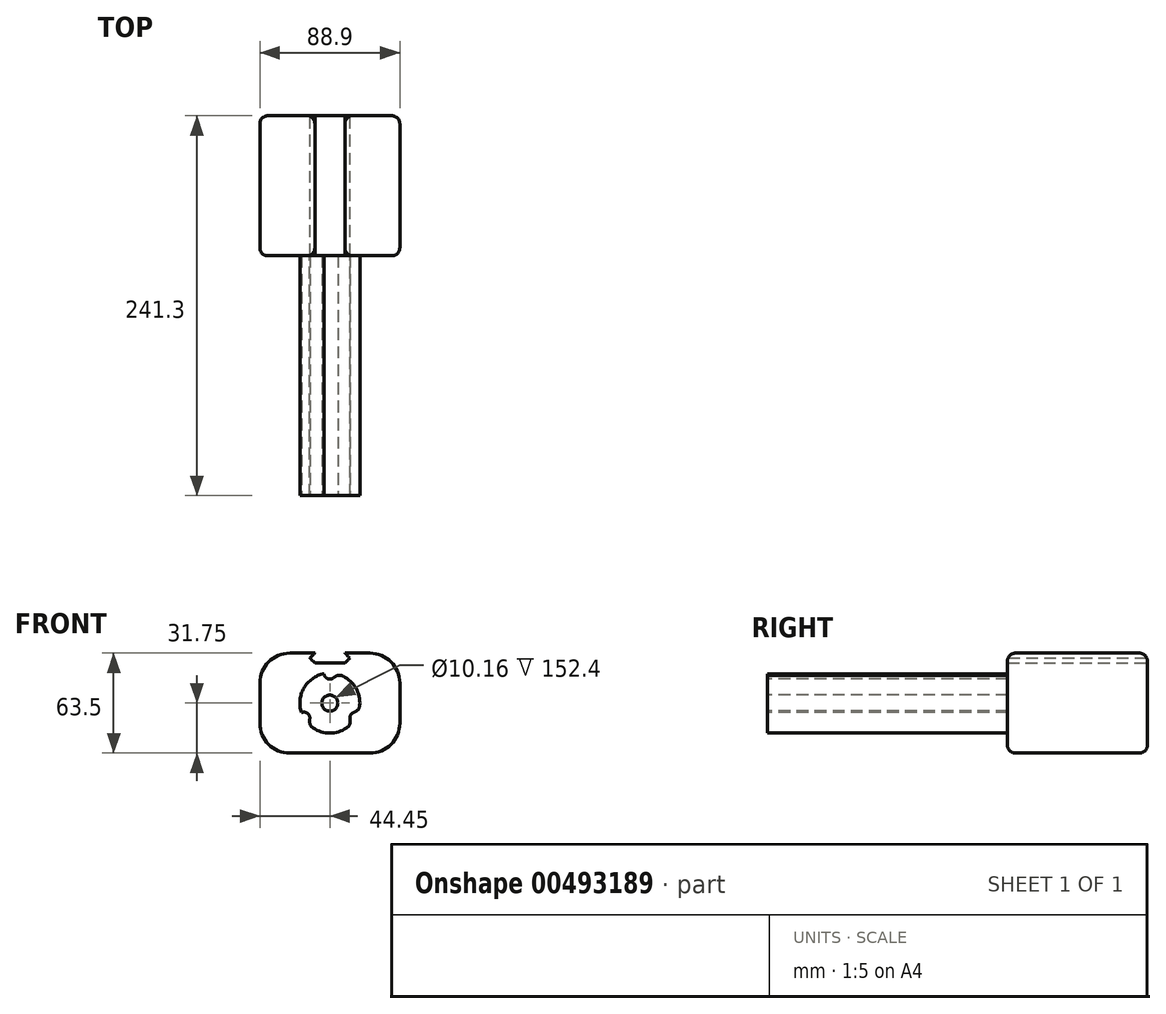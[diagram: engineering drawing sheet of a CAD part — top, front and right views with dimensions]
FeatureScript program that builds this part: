
annotation { "Feature Type Name" : "Feature", "Feature Type Description" : "" }
export const myFeature = defineFeature(function(context is Context, id is Id, definition is map)
    precondition{}
    {
        {
            var Q0;
            Q0=qCreatedBy(makeId("Front.planeOp"),FACE);
            var sketch = newSketch(context, id + "F0", { "sketchPlane" : qUnion([Q0])});
            skCircle(sketch, "E0", {"center": v(0, 0) * mm, "radius": 19.05 * mm});
            skSolve(sketch);
        }
        {
            var Q0;
            Q0 = qSketchRegion(id + "F0", true);
            extrude(context, id + "F1", {"entities" : qUnion([Q0]), "depth" : 152.4 * mm});
        }
        {
            var Q0;
            Q0=makeQuery(id+"F1.opExtrude","CAP_FACE",FACE,{"disambiguationData":[OSD([sQuery(id+"F0.wireOp",EDGE,"E0")])],"isStart":true});
            var sketch = newSketch(context, id + "F2", { "sketchPlane" : qUnion([Q0])});
            skLineSegment(sketch, "E1.bottom", {"start": v(-44.45, 31.75) * mm, "end": v(44.45, 31.75) * mm});
            skLineSegment(sketch, "E1.top", {"start": v(-44.45, -31.75) * mm, "end": v(44.45, -31.75) * mm});
            skLineSegment(sketch, "E1.left", {"start": v(-44.45, 31.75) * mm, "end": v(-44.45, -31.75) * mm});
            skLineSegment(sketch, "E1.right", {"start": v(44.45, 31.75) * mm, "end": v(44.45, -31.75) * mm});
            skPoint(sketch, "E1.middle", {"position": v(0, 0) * mm});
            skSolve(sketch);
        }
        {
            var Q0;
            Q0 = qSketchRegion(id + "F2", true);
            extrude(context, id + "F3", {"entities" : qUnion([Q0]), "operationType" : NewBodyOperationType.ADD, "depth" : 88.9 * mm});
        }
        {
            var Q0;
            Q0=makeQuery(id+"F3.opExtrude","SWEPT_EDGE",EDGE,{"disambiguationData":[OSD([sQuery(id+"F2.wireOp",EDGE,"E1.bottom"),sQuery(id+"F2.wireOp",EDGE,"E1.left")])]});
            var Q1;
            Q1=makeQuery(id+"F3.opExtrude","SWEPT_EDGE",EDGE,{"disambiguationData":[OSD([sQuery(id+"F2.wireOp",EDGE,"E1.bottom"),sQuery(id+"F2.wireOp",EDGE,"E1.right")])]});
            var Q2;
            Q2=makeQuery(id+"F3.opExtrude","SWEPT_EDGE",EDGE,{"disambiguationData":[OSD([sQuery(id+"F2.wireOp",EDGE,"E1.top"),sQuery(id+"F2.wireOp",EDGE,"E1.right")])]});
            var Q3;
            Q3=makeQuery(id+"F3.opExtrude","SWEPT_EDGE",EDGE,{"disambiguationData":[OSD([sQuery(id+"F2.wireOp",EDGE,"E1.top"),sQuery(id+"F2.wireOp",EDGE,"E1.left")])]});
            fillet(context, id + "F4", {"entities" : qUnion([Q0, Q1, Q2, Q3]), "radius" : 19.05 * mm, "tangentPropagation" : true, "allowEdgeOverflow" : false});
        }
        {
            var Q0;
            Q0=makeQuery(id+"F1.opExtrude","CAP_FACE",FACE,{"disambiguationData":[OSD([sQuery(id+"F0.wireOp",EDGE,"E0")])],"isStart":false});
            var sketch = newSketch(context, id + "F5", { "sketchPlane" : qUnion([Q0])});
            skCircle(sketch, "E2", {"center": v(0, 0) * mm, "radius": 5.08 * mm});
            skArc(sketch, "E3", {"start": v(-3.8, 18.67) * mm, "mid": v(0, 15.24) * mm, "end": v(3.8, 18.67) * mm});
            skArc(sketch, "E4.0", {"start": v(3.8, 18.67) * mm, "mid": v(0, 19.05) * mm, "end": v(-3.8, 18.67) * mm});
            skArc(sketch, "E5.1.0", {"start": v(-14.27, -12.62) * mm, "mid": v(-13.2, -7.62) * mm, "end": v(-18.06, -6.05) * mm});
            skArc(sketch, "E5.1.1", {"start": v(-18.06, -6.05) * mm, "mid": v(-16.5, -9.52) * mm, "end": v(-14.27, -12.62) * mm});
            skArc(sketch, "E5.2.0", {"start": v(18.06, -6.05) * mm, "mid": v(13.2, -7.62) * mm, "end": v(14.27, -12.62) * mm});
            skArc(sketch, "E5.2.1", {"start": v(14.27, -12.62) * mm, "mid": v(16.5, -9.53) * mm, "end": v(18.06, -6.05) * mm});
            skSolve(sketch);
        }
        {
            var Q0;
            Q0 = qSketchRegion(id + "F5", true);
            var Q1;
            Q1=makeQuery(id+"F3.opExtrude","CAP_FACE",FACE,{"disambiguationData":[OSD([sQuery(id+"F2.wireOp",EDGE,"E1.bottom"),sQuery(id+"F2.wireOp",EDGE,"E1.top"),sQuery(id+"F2.wireOp",EDGE,"E1.left"),sQuery(id+"F2.wireOp",EDGE,"E1.right")])],"isStart":true});
            extrude(context, id + "F6", {"entities" : qUnion([Q0]), "operationType" : NewBodyOperationType.REMOVE, "endBound" : BoundingType.UP_TO_SURFACE, "oppositeDirection" : true, "endBoundEntityFace" : qUnion([Q1]), "depth" : 25.4 * mm});
        }
        {
            var Q0;
            Q0=makeQuery(id+"F3.opExtrude","CAP_FACE",FACE,{"disambiguationData":[OSD([sQuery(id+"F2.wireOp",EDGE,"E1.bottom"),sQuery(id+"F2.wireOp",EDGE,"E1.top"),sQuery(id+"F2.wireOp",EDGE,"E1.left"),sQuery(id+"F2.wireOp",EDGE,"E1.right")])],"isStart":false});
            var sketch = newSketch(context, id + "F7", { "sketchPlane" : qUnion([Q0])});
            skLineSegment(sketch, "E6", {"start": v(0, 0) * mm, "end": v(0, 37.97) * mm, "construction": true});
            skPoint(sketch, "E6.endSnap0", {"position": v(0, 31.75) * mm});
            skLineSegment(sketch, "E7", {"start": v(0, 31.75) * mm, "end": v(-9.52, 31.75) * mm});
            skLineSegment(sketch, "E8", {"start": v(-9.52, 31.75) * mm, "end": v(-12.7, 28.58) * mm});
            skLineSegment(sketch, "E9", {"start": v(-12.7, 28.58) * mm, "end": v(-9.52, 25.4) * mm});
            skLineSegment(sketch, "E10", {"start": v(-9.52, 25.4) * mm, "end": v(0, 25.4) * mm});
            skLineSegment(sketch, "E11.MirrorCS", {"start": v(9.53, 25.4) * mm, "end": v(0, 25.4) * mm});
            skLineSegment(sketch, "E12.MirrorCS", {"start": v(12.7, 28.58) * mm, "end": v(9.53, 25.4) * mm});
            skLineSegment(sketch, "E13.MirrorCS", {"start": v(9.53, 31.75) * mm, "end": v(12.7, 28.58) * mm});
            skLineSegment(sketch, "E14.MirrorCS", {"start": v(0, 31.75) * mm, "end": v(9.53, 31.75) * mm});
            skSolve(sketch);
        }
        {
            var Q0;
            Q0 = qSketchRegion(id + "F7", true);
            extrude(context, id + "F8", {"entities" : qUnion([Q0]), "operationType" : NewBodyOperationType.REMOVE, "endBound" : BoundingType.THROUGH_ALL, "oppositeDirection" : true, "depth" : 25.4 * mm});
        }
        {
            var Q0;
            {var subQ0=sQuery(id+"F5.wireOp",EDGE,"E4.0");var subQ1=sQuery(id+"F5.wireOp",EDGE,"E3");var subQ2=sQuery(id+"F0.wireOp",EDGE,"E0");Q0=makeQuery(id+"F6.boolean.opBoolean","COPY",EDGE,{"derivedFrom":makeQuery(id+"F6.opExtrude","SWEPT_EDGE",EDGE,{"disambiguationData":[OSD([subQ2,subQ1,subQ0]),TDD([makeQuery(id+"F5.imprint","INTERSECT",VERTEX,{"disambiguationData":[OD(0.0)],"derivedFrom":[makeQuery(id+"F1.opExtrude","CAP_EDGE",EDGE,{"disambiguationData":[OSD([subQ2])],"isStart":false}),subQ1,subQ0]})])]})});}
            var Q1;
            {var subQ0=sQuery(id+"F5.wireOp",EDGE,"E4.0");var subQ1=sQuery(id+"F5.wireOp",EDGE,"E3");var subQ2=sQuery(id+"F0.wireOp",EDGE,"E0");Q1=makeQuery(id+"F6.boolean.opBoolean","COPY",EDGE,{"derivedFrom":makeQuery(id+"F6.opExtrude","SWEPT_EDGE",EDGE,{"disambiguationData":[OSD([subQ2,subQ1,subQ0]),TDD([makeQuery(id+"F5.imprint","INTERSECT",VERTEX,{"disambiguationData":[OD(1.0)],"derivedFrom":[makeQuery(id+"F1.opExtrude","CAP_EDGE",EDGE,{"disambiguationData":[OSD([subQ2])],"isStart":false}),subQ1,subQ0]})])]})});}
            var Q2;
            {var subQ0=sQuery(id+"F5.wireOp",EDGE,"E5.1.1");var subQ1=sQuery(id+"F5.wireOp",EDGE,"E5.1.0");var subQ2=sQuery(id+"F0.wireOp",EDGE,"E0");Q2=makeQuery(id+"F6.boolean.opBoolean","COPY",EDGE,{"derivedFrom":makeQuery(id+"F6.opExtrude","SWEPT_EDGE",EDGE,{"disambiguationData":[OSD([subQ2,subQ1,subQ0]),TDD([makeQuery(id+"F5.imprint","INTERSECT",VERTEX,{"disambiguationData":[OD(1.0)],"derivedFrom":[makeQuery(id+"F1.opExtrude","CAP_EDGE",EDGE,{"disambiguationData":[OSD([subQ2])],"isStart":false}),subQ1,subQ0]})])]})});}
            var Q3;
            {var subQ0=sQuery(id+"F5.wireOp",EDGE,"E5.1.1");var subQ1=sQuery(id+"F5.wireOp",EDGE,"E5.1.0");var subQ2=sQuery(id+"F0.wireOp",EDGE,"E0");Q3=makeQuery(id+"F6.boolean.opBoolean","COPY",EDGE,{"derivedFrom":makeQuery(id+"F6.opExtrude","SWEPT_EDGE",EDGE,{"disambiguationData":[OSD([subQ2,subQ1,subQ0]),TDD([makeQuery(id+"F5.imprint","INTERSECT",VERTEX,{"disambiguationData":[OD(0.0)],"derivedFrom":[makeQuery(id+"F1.opExtrude","CAP_EDGE",EDGE,{"disambiguationData":[OSD([subQ2])],"isStart":false}),subQ1,subQ0]})])]})});}
            var Q4;
            {var subQ0=sQuery(id+"F5.wireOp",EDGE,"E5.2.1");var subQ1=sQuery(id+"F5.wireOp",EDGE,"E5.2.0");var subQ2=sQuery(id+"F0.wireOp",EDGE,"E0");Q4=makeQuery(id+"F6.boolean.opBoolean","COPY",EDGE,{"derivedFrom":makeQuery(id+"F6.opExtrude","SWEPT_EDGE",EDGE,{"disambiguationData":[OSD([subQ2,subQ1,subQ0]),TDD([makeQuery(id+"F5.imprint","INTERSECT",VERTEX,{"disambiguationData":[OD(1.0)],"derivedFrom":[makeQuery(id+"F1.opExtrude","CAP_EDGE",EDGE,{"disambiguationData":[OSD([subQ2])],"isStart":false}),subQ1,subQ0]})])]})});}
            var Q5;
            {var subQ0=sQuery(id+"F5.wireOp",EDGE,"E5.2.1");var subQ1=sQuery(id+"F5.wireOp",EDGE,"E5.2.0");var subQ2=sQuery(id+"F0.wireOp",EDGE,"E0");Q5=makeQuery(id+"F6.boolean.opBoolean","COPY",EDGE,{"derivedFrom":makeQuery(id+"F6.opExtrude","SWEPT_EDGE",EDGE,{"disambiguationData":[OSD([subQ2,subQ1,subQ0]),TDD([makeQuery(id+"F5.imprint","INTERSECT",VERTEX,{"disambiguationData":[OD(0.0)],"derivedFrom":[makeQuery(id+"F1.opExtrude","CAP_EDGE",EDGE,{"disambiguationData":[OSD([subQ2])],"isStart":false}),subQ1,subQ0]})])]})});}
            fillet(context, id + "F9", {"entities" : qUnion([Q0, Q1, Q2, Q3, Q4, Q5]), "radius" : 5.08 * mm, "tangentPropagation" : true, "allowEdgeOverflow" : false});
        }
        {
            var Q0;
            Q0=makeQuery(id+"F3.opExtrude","CAP_EDGE",EDGE,{"disambiguationData":[OSD([sQuery(id+"F2.wireOp",EDGE,"E1.left")])],"isStart":true});
            var Q1;
            Q1=makeQuery(id+"F3.opExtrude","CAP_EDGE",EDGE,{"disambiguationData":[OSD([sQuery(id+"F2.wireOp",EDGE,"E1.left")])],"isStart":false});
            fillet(context, id + "F10", {"entities" : qUnion([Q0, Q1]), "radius" : 5.08 * mm, "tangentPropagation" : true, "allowEdgeOverflow" : false});
        }
    });
